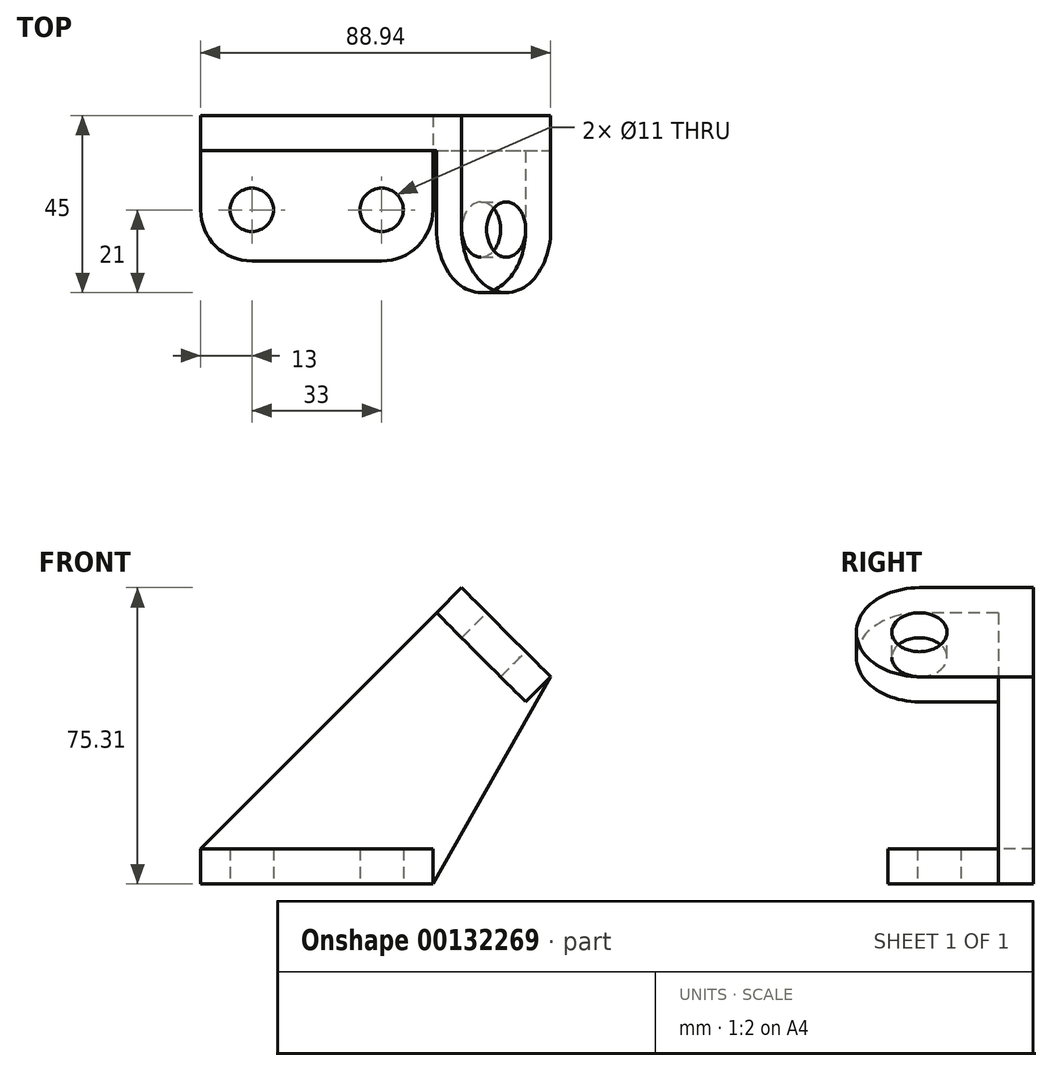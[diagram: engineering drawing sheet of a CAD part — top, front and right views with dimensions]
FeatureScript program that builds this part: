
annotation { "Feature Type Name" : "Feature", "Feature Type Description" : "" }
export const myFeature = defineFeature(function(context is Context, id is Id, definition is map)
    precondition{}
    {
        {
            var Q0;
            Q0=qCreatedBy(makeId("Top.planeOp"),FACE);
            var sketch = newSketch(context, id + "F0", { "sketchPlane" : qUnion([Q0])});
            skCircle(sketch, "E0", {"center": v(0, 0) * mm, "radius": 5.5 * mm});
            skCircle(sketch, "E1", {"center": v(33, 0) * mm, "radius": 5.5 * mm});
            skLineSegment(sketch, "E2", {"start": v(46, 15) * mm, "end": v(-13, 15) * mm});
            skLineSegment(sketch, "E3", {"start": v(-13, 15) * mm, "end": v(-13, 0) * mm});
            skLineSegment(sketch, "E4", {"start": v(0, -13) * mm, "end": v(33, -13) * mm});
            skLineSegment(sketch, "E5", {"start": v(46, 0) * mm, "end": v(46, 15) * mm});
            skPoint(sketch, "E6.visualSharp", {"position": v(46, -13) * mm});
            skArc(sketch, "E6.filletArc", {"start": v(33, -13) * mm, "mid": v(42.2, -9.2) * mm, "end": v(46, 0) * mm});
            skPoint(sketch, "E7.visualSharp", {"position": v(-13, -13) * mm});
            skArc(sketch, "E7.filletArc", {"start": v(-13, 0) * mm, "mid": v(-9.2, -9.2) * mm, "end": v(0, -13) * mm});
            skSolve(sketch);
        }
        {
            var Q0;
            Q0 = qSketchRegion(id + "F0", true);
            extrude(context, id + "F1", {"entities" : qUnion([Q0]), "depth" : 9 * mm});
        }
        {
            var Q0;
            Q0=makeQuery(id+"F1.opExtrude","SWEPT_FACE",FACE,{"disambiguationData":[OSD([sQuery(id+"F0.wireOp",EDGE,"E2")])]});
            var sketch = newSketch(context, id + "F2", { "sketchPlane" : qUnion([Q0])});
            skLineSegment(sketch, "E8", {"start": v(13, 9) * mm, "end": v(13, 0) * mm});
            skLineSegment(sketch, "E9", {"start": v(13, 0) * mm, "end": v(-46, 0) * mm});
            skLineSegment(sketch, "E10", {"start": v(-46, 0) * mm, "end": v(-75.94, 52.69) * mm});
            skLineSegment(sketch, "E11", {"start": v(-75.94, 52.69) * mm, "end": v(-53.31, 75.31) * mm});
            skLineSegment(sketch, "E12", {"start": v(-53.31, 75.31) * mm, "end": v(13, 9) * mm});
            skLineSegment(sketch, "E13", {"start": v(-64.63, 64) * mm, "end": v(-84.88, 64) * mm, "construction": true});
            skSolve(sketch);
        }
        {
            var Q0;
            Q0 = qSketchRegion(id + "F2", true);
            extrude(context, id + "F3", {"entities" : qUnion([Q0]), "operationType" : NewBodyOperationType.ADD, "depth" : 9 * mm});
        }
        {
            var Q0;
            Q0=makeQuery(id+"F3.opExtrude","SWEPT_FACE",FACE,{"disambiguationData":[OSD([sQuery(id+"F2.wireOp",EDGE,"E11")])]});
            var sketch = newSketch(context, id + "F4", { "sketchPlane" : qUnion([Q0])});
            skLineSegment(sketch, "E14", {"start": v(24, 15.56) * mm, "end": v(24, -16.44) * mm});
            skLineSegment(sketch, "E15", {"start": v(24, -16.44) * mm, "end": v(-5, -16.44) * mm});
            skLineSegment(sketch, "E16", {"start": v(24, 15.56) * mm, "end": v(-5, 15.56) * mm});
            skArc(sketch, "E17", {"start": v(-5, 15.56) * mm, "mid": v(-21, -0.44) * mm, "end": v(-5, -16.44) * mm});
            skCircle(sketch, "E18", {"center": v(-5, -0.44) * mm, "radius": 7 * mm});
            skSolve(sketch);
        }
        {
            var Q0;
            Q0 = qSketchRegion(id + "F4", true);
            extrude(context, id + "F5", {"entities" : qUnion([Q0]), "operationType" : NewBodyOperationType.ADD, "oppositeDirection" : true, "depth" : 9 * mm});
        }
    });
